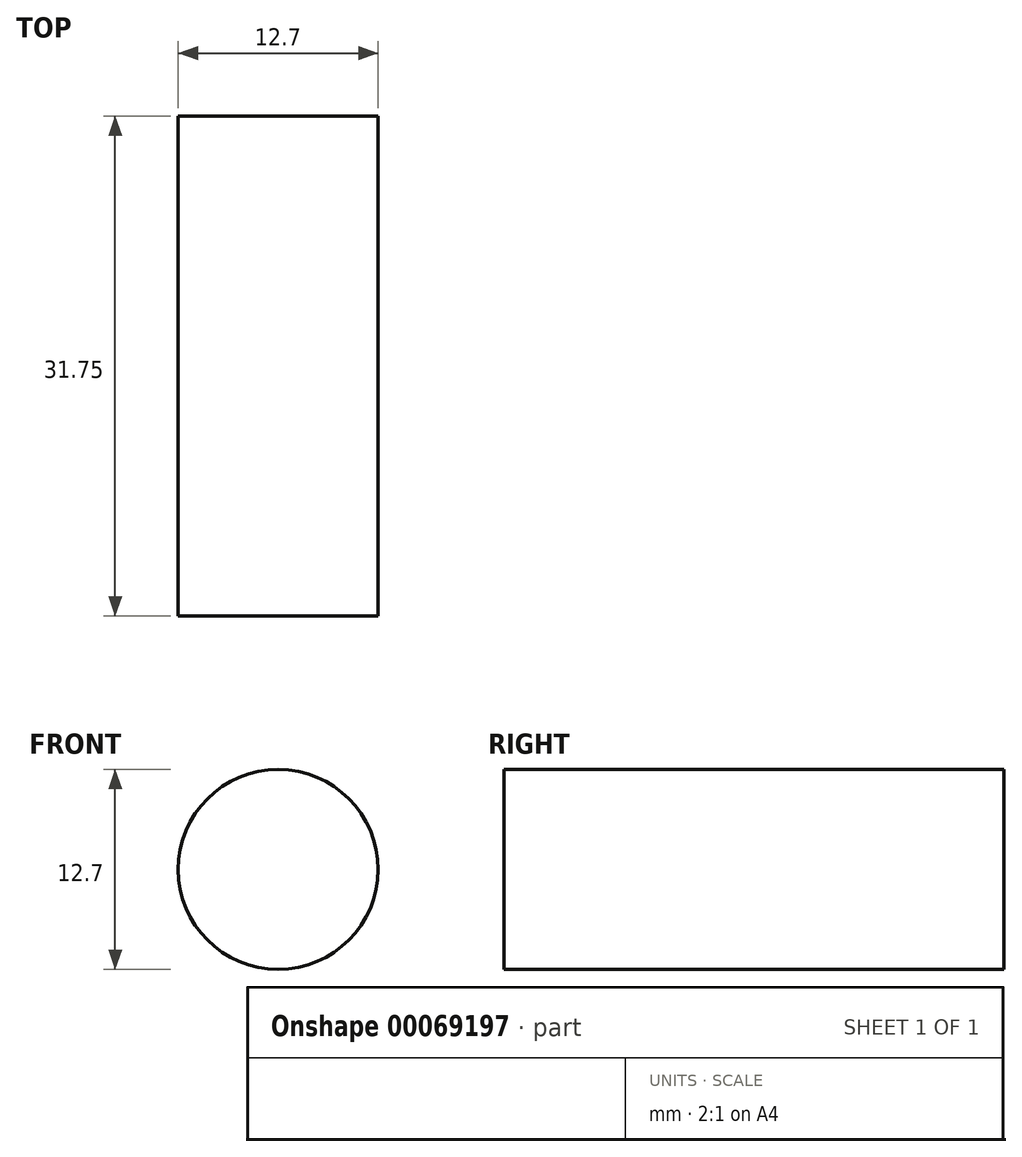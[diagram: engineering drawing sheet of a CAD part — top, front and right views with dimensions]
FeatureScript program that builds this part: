
annotation { "Feature Type Name" : "Feature", "Feature Type Description" : "" }
export const myFeature = defineFeature(function(context is Context, id is Id, definition is map)
    precondition{}
    {
        {
            var Q0;
            Q0=qCreatedBy(makeId("Front.planeOp"),FACE);
            var sketch = newSketch(context, id + "F0", { "sketchPlane" : qUnion([Q0])});
            skCircle(sketch, "E0", {"center": v(0, 0) * mm, "radius": 6.35 * mm});
            skSolve(sketch);
        }
        {
            var Q0;
            Q0 = qSketchRegion(id + "F0", true);
            extrude(context, id + "F1", {"entities" : qUnion([Q0]), "depth" : 31.75 * mm});
        }
    });
